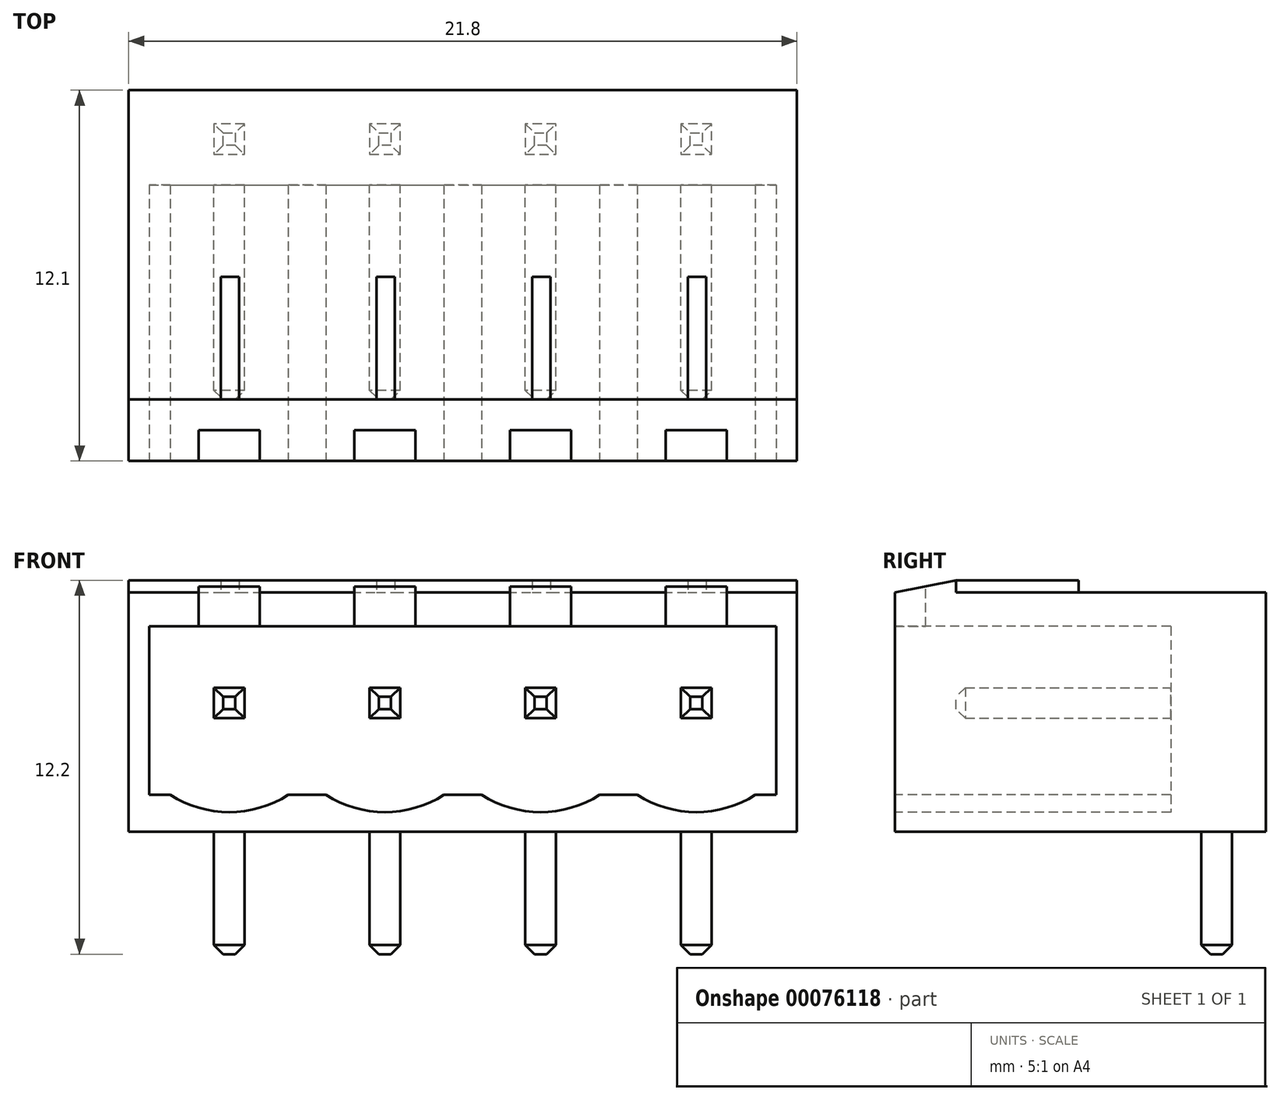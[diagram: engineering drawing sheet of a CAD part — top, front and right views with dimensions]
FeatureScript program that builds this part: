
annotation { "Feature Type Name" : "Feature", "Feature Type Description" : "" }
export const myFeature = defineFeature(function(context is Context, id is Id, definition is map)
    precondition{}
    {
        {
            var Q0;
            Q0=qCreatedBy(makeId("Front.planeOp"),FACE);
            var sketch = newSketch(context, id + "F0", { "sketchPlane" : qUnion([Q0])});
            skLineSegment(sketch, "E0.bottom", {"start": v(-10.9, 4.1) * mm, "end": v(10.9, 4.1) * mm});
            skLineSegment(sketch, "E0.top", {"start": v(-10.9, -4.1) * mm, "end": v(10.9, -4.1) * mm});
            skLineSegment(sketch, "E0.left", {"start": v(-10.9, 4.1) * mm, "end": v(-10.9, -4.1) * mm});
            skLineSegment(sketch, "E0.right", {"start": v(10.9, 4.1) * mm, "end": v(10.9, -4.1) * mm});
            skPoint(sketch, "E0.middle", {"position": v(0, 0) * mm});
            skSolve(sketch);
        }
        {
            var Q0;
            Q0=makeQuery(id+"F0.imprint","IMPRINT",FACE,{"disambiguationData":[TD([[makeQuery(id+"F0.imprint","IMPRINT",EDGE,{"derivedFrom":sQuery(id+"F0.wireOp",EDGE,"E0.bottom")}),-1.0]])]});
            extrude(context, id + "F1", {"entities" : qUnion([Q0]), "depth" : 12.1 * mm, "symmetric" : true});
        }
        {
            var Q0;
            Q0=makeQuery(id+"F1.opExtrude","CAP_FACE",FACE,{"disambiguationData":[OSD([sQuery(id+"F0.wireOp",EDGE,"E0.bottom"),sQuery(id+"F0.wireOp",EDGE,"E0.top"),sQuery(id+"F0.wireOp",EDGE,"E0.left"),sQuery(id+"F0.wireOp",EDGE,"E0.right")])],"isStart":false});
            var sketch = newSketch(context, id + "F2", { "sketchPlane" : qUnion([Q0])});
            skPoint(sketch, "E1.middle", {"position": v(0, 0) * mm});
            skLineSegment(sketch, "E2.bottom", {"start": v(-10.23, 2.6) * mm, "end": v(10.23, 2.6) * mm});
            skLineSegment(sketch, "E2.top", {"start": v(-10.23, -2.4) * mm, "end": v(10.23, -2.4) * mm, "construction": true});
            skLineSegment(sketch, "E2.left", {"start": v(-10.23, 2.6) * mm, "end": v(-10.23, -2.4) * mm});
            skLineSegment(sketch, "E2.right", {"start": v(10.23, 2.6) * mm, "end": v(10.23, -2.4) * mm});
            skPoint(sketch, "E3", {"position": v(-2.54, 0.1) * mm});
            skPoint(sketch, "E4", {"position": v(-7.62, 0.1) * mm});
            skLineSegment(sketch, "E5", {"start": v(-10.23, 0.1) * mm, "end": v(10.23, 0.1) * mm, "construction": true});
            skArc(sketch, "E6", {"start": v(0, -2.4) * mm, "mid": v(-2.54, -3.46) * mm, "end": v(-5.08, -2.4) * mm});
            skArc(sketch, "E7", {"start": v(-5.08, -2.4) * mm, "mid": v(-7.62, -3.46) * mm, "end": v(-10.16, -2.4) * mm});
            skLineSegment(sketch, "E8", {"start": v(0, 12.68) * mm, "end": v(0, -9.6) * mm, "construction": true});
            skPoint(sketch, "E9", {"position": v(2.54, 0.1) * mm});
            skPoint(sketch, "E10", {"position": v(7.62, 0.1) * mm});
            skPoint(sketch, "E11", {"position": v(0, 9.54) * mm});
            skArc(sketch, "E12", {"start": v(0, -2.4) * mm, "mid": v(2.54, -3.46) * mm, "end": v(5.08, -2.4) * mm});
            skArc(sketch, "E13", {"start": v(5.08, -2.4) * mm, "mid": v(7.62, -3.46) * mm, "end": v(10.16, -2.4) * mm});
            skLineSegment(sketch, "E14", {"start": v(10.23, -2.4) * mm, "end": v(10.16, -2.4) * mm});
            skLineSegment(sketch, "E15", {"start": v(-10.16, -2.4) * mm, "end": v(-10.23, -2.4) * mm});
            skSolve(sketch);
        }
        {
            var Q0;
            Q0 = qSketchRegion(id + "F2", true);
            extrude(context, id + "F3", {"entities" : qUnion([Q0]), "operationType" : NewBodyOperationType.REMOVE, "oppositeDirection" : true, "depth" : 9 * mm});
        }
        {
            var Q0;
            Q0=makeQuery(id+"F3.boolean.opBoolean","COPY",FACE,{"derivedFrom":makeQuery(id+"F3.opExtrude","CAP_FACE",FACE,{"disambiguationData":[OSD([sQuery(id+"F2.wireOp",EDGE,"E2.bottom"),sQuery(id+"F2.wireOp",EDGE,"E2.left"),sQuery(id+"F2.wireOp",EDGE,"E2.right"),sQuery(id+"F2.wireOp",EDGE,"E6"),sQuery(id+"F2.wireOp",EDGE,"E7"),sQuery(id+"F2.wireOp",EDGE,"E12"),sQuery(id+"F2.wireOp",EDGE,"E13"),sQuery(id+"F2.wireOp",EDGE,"E14"),sQuery(id+"F2.wireOp",EDGE,"E15")])],"isStart":false})});
            var sketch = newSketch(context, id + "F4", { "sketchPlane" : qUnion([Q0])});
            skLineSegment(sketch, "E16.bottom", {"start": v(-7.12, -0.4) * mm, "end": v(-8.12, -0.4) * mm});
            skLineSegment(sketch, "E16.top", {"start": v(-7.12, 0.6) * mm, "end": v(-8.12, 0.6) * mm});
            skLineSegment(sketch, "E16.left", {"start": v(-7.12, -0.4) * mm, "end": v(-7.12, 0.6) * mm});
            skLineSegment(sketch, "E16.right", {"start": v(-8.12, -0.4) * mm, "end": v(-8.12, 0.6) * mm});
            skPoint(sketch, "E16.middle", {"position": v(-7.62, 0.1) * mm});
            skLineSegment(sketch, "E17.bottom", {"start": v(-2.04, -0.4) * mm, "end": v(-3.04, -0.4) * mm});
            skLineSegment(sketch, "E17.top", {"start": v(-2.04, 0.6) * mm, "end": v(-3.04, 0.6) * mm});
            skLineSegment(sketch, "E17.left", {"start": v(-2.04, -0.4) * mm, "end": v(-2.04, 0.6) * mm});
            skLineSegment(sketch, "E17.right", {"start": v(-3.04, -0.4) * mm, "end": v(-3.04, 0.6) * mm});
            skPoint(sketch, "E17.middle", {"position": v(-2.54, 0.1) * mm});
            skLineSegment(sketch, "E18.bottom", {"start": v(3.04, -0.4) * mm, "end": v(2.04, -0.4) * mm});
            skLineSegment(sketch, "E18.top", {"start": v(3.04, 0.6) * mm, "end": v(2.04, 0.6) * mm});
            skLineSegment(sketch, "E18.left", {"start": v(3.04, -0.4) * mm, "end": v(3.04, 0.6) * mm});
            skLineSegment(sketch, "E18.right", {"start": v(2.04, -0.4) * mm, "end": v(2.04, 0.6) * mm});
            skPoint(sketch, "E18.middle", {"position": v(2.54, 0.1) * mm});
            skLineSegment(sketch, "E19.bottom", {"start": v(8.12, -0.4) * mm, "end": v(7.12, -0.4) * mm});
            skLineSegment(sketch, "E19.top", {"start": v(8.12, 0.6) * mm, "end": v(7.12, 0.6) * mm});
            skLineSegment(sketch, "E19.left", {"start": v(8.12, -0.4) * mm, "end": v(8.12, 0.6) * mm});
            skLineSegment(sketch, "E19.right", {"start": v(7.12, -0.4) * mm, "end": v(7.12, 0.6) * mm});
            skPoint(sketch, "E19.middle", {"position": v(7.62, 0.1) * mm});
            skLineSegment(sketch, "E20", {"start": v(10.9, 0.1) * mm, "end": v(-10.9, 0.1) * mm, "construction": true});
            skPoint(sketch, "E20.startSnap0", {"position": v(10.23, 0.1) * mm});
            skPoint(sketch, "E20.endSnap0", {"position": v(-10.23, 0.1) * mm});
            skLineSegment(sketch, "E21", {"start": v(0, 4.1) * mm, "end": v(0, -4.1) * mm, "construction": true});
            skPoint(sketch, "E21.startSnap0", {"position": v(0, 2.6) * mm});
            skSolve(sketch);
        }
        {
            var Q0;
            Q0 = qSketchRegion(id + "F4", true);
            var Q1;
            Q1=makeQuery(id+"F1.opExtrude","CAP_FACE",FACE,{"disambiguationData":[OSD([sQuery(id+"F0.wireOp",EDGE,"E0.bottom"),sQuery(id+"F0.wireOp",EDGE,"E0.top"),sQuery(id+"F0.wireOp",EDGE,"E0.left"),sQuery(id+"F0.wireOp",EDGE,"E0.right")])],"isStart":false});
            extrude(context, id + "F5", {"entities" : qUnion([Q0]), "endBoundEntityFace" : qUnion([Q1]), "depth" : 7 * mm});
        }
        {
            var Q0;
            Q0=makeQuery(id+"F1.opExtrude","SWEPT_FACE",FACE,{"disambiguationData":[OSD([sQuery(id+"F0.wireOp",EDGE,"E0.top")])]});
            var sketch = newSketch(context, id + "F6", { "sketchPlane" : qUnion([Q0])});
            skLineSegment(sketch, "E22", {"start": v(0, 6.05) * mm, "end": v(0, -6.05) * mm, "construction": true});
            skLineSegment(sketch, "E23.bottom", {"start": v(-8.12, -3.95) * mm, "end": v(-7.12, -3.95) * mm});
            skLineSegment(sketch, "E23.top", {"start": v(-8.12, -4.95) * mm, "end": v(-7.12, -4.95) * mm});
            skLineSegment(sketch, "E23.left", {"start": v(-8.12, -3.95) * mm, "end": v(-8.12, -4.95) * mm});
            skLineSegment(sketch, "E23.right", {"start": v(-7.12, -3.95) * mm, "end": v(-7.12, -4.95) * mm});
            skPoint(sketch, "E23.middle", {"position": v(-7.62, -4.45) * mm});
            skLineSegment(sketch, "E24.bottom", {"start": v(-3.04, -3.95) * mm, "end": v(-2.04, -3.95) * mm});
            skLineSegment(sketch, "E24.top", {"start": v(-3.04, -4.95) * mm, "end": v(-2.04, -4.95) * mm});
            skLineSegment(sketch, "E24.left", {"start": v(-3.04, -3.95) * mm, "end": v(-3.04, -4.95) * mm});
            skLineSegment(sketch, "E24.right", {"start": v(-2.04, -3.95) * mm, "end": v(-2.04, -4.95) * mm});
            skPoint(sketch, "E24.middle", {"position": v(-2.54, -4.45) * mm});
            skLineSegment(sketch, "E25", {"start": v(-10.9, -4.45) * mm, "end": v(10.9, -4.45) * mm, "construction": true});
            skPoint(sketch, "E25.startSnap0", {"position": v(-8.12, -4.45) * mm});
            skLineSegment(sketch, "E26.MirrorCS", {"start": v(8.12, -3.95) * mm, "end": v(8.12, -4.95) * mm});
            skLineSegment(sketch, "E27.MirrorCS", {"start": v(7.12, -3.95) * mm, "end": v(7.12, -4.95) * mm});
            skLineSegment(sketch, "E28.MirrorCS", {"start": v(3.04, -3.95) * mm, "end": v(2.04, -3.95) * mm});
            skLineSegment(sketch, "E29.MirrorCS", {"start": v(3.04, -4.95) * mm, "end": v(2.04, -4.95) * mm});
            skLineSegment(sketch, "E30.MirrorCS", {"start": v(8.12, -4.95) * mm, "end": v(7.12, -4.95) * mm});
            skPoint(sketch, "E31.MirrorP", {"position": v(2.54, -4.45) * mm});
            skLineSegment(sketch, "E32.MirrorCS", {"start": v(3.04, -3.95) * mm, "end": v(3.04, -4.95) * mm});
            skLineSegment(sketch, "E33.MirrorCS", {"start": v(2.04, -3.95) * mm, "end": v(2.04, -4.95) * mm});
            skPoint(sketch, "E34.MirrorP", {"position": v(8.12, -4.45) * mm});
            skPoint(sketch, "E35.MirrorP", {"position": v(7.62, -4.45) * mm});
            skLineSegment(sketch, "E36.MirrorCS", {"start": v(8.12, -3.95) * mm, "end": v(7.12, -3.95) * mm});
            skSolve(sketch);
        }
        {
            var Q0;
            Q0 = qSketchRegion(id + "F6", true);
            extrude(context, id + "F7", {"entities" : qUnion([Q0]), "depth" : 4 * mm});
        }
        {
            var Q0;
            Q0=makeQuery(id+"F1.opExtrude","SWEPT_FACE",FACE,{"disambiguationData":[OSD([sQuery(id+"F0.wireOp",EDGE,"E0.bottom")])]});
            var sketch = newSketch(context, id + "F8", { "sketchPlane" : qUnion([Q0])});
            skLineSegment(sketch, "E37", {"start": v(0, 6.05) * mm, "end": v(0, -6.05) * mm, "construction": true});
            skLineSegment(sketch, "E38.bottom", {"start": v(-3.54, -5.05) * mm, "end": v(-1.54, -5.05) * mm});
            skLineSegment(sketch, "E38.top", {"start": v(-3.54, -6.05) * mm, "end": v(-1.54, -6.05) * mm});
            skLineSegment(sketch, "E38.left", {"start": v(-3.54, -5.05) * mm, "end": v(-3.54, -6.05) * mm});
            skLineSegment(sketch, "E38.right", {"start": v(-1.54, -5.05) * mm, "end": v(-1.54, -6.05) * mm});
            skPoint(sketch, "E38.middle", {"position": v(-2.54, -5.55) * mm});
            skLineSegment(sketch, "E39.1.0.0", {"start": v(3.54, -5.05) * mm, "end": v(3.54, -6.05) * mm});
            skLineSegment(sketch, "E39.1.0.1", {"start": v(1.54, -5.05) * mm, "end": v(1.54, -6.05) * mm});
            skLineSegment(sketch, "E39.1.0.2", {"start": v(1.54, -6.05) * mm, "end": v(3.54, -6.05) * mm});
            skLineSegment(sketch, "E39.1.0.3", {"start": v(1.54, -5.05) * mm, "end": v(3.54, -5.05) * mm});
            skPoint(sketch, "E39.1.0.4", {"position": v(2.54, -5.55) * mm});
            skLineSegment(sketch, "E39.2.0.0", {"start": v(8.62, -5.05) * mm, "end": v(8.62, -6.05) * mm});
            skLineSegment(sketch, "E39.2.0.1", {"start": v(6.62, -5.05) * mm, "end": v(6.62, -6.05) * mm});
            skLineSegment(sketch, "E39.2.0.2", {"start": v(6.62, -6.05) * mm, "end": v(8.62, -6.05) * mm});
            skLineSegment(sketch, "E39.2.0.3", {"start": v(6.62, -5.05) * mm, "end": v(8.62, -5.05) * mm});
            skPoint(sketch, "E39.2.0.4", {"position": v(7.62, -5.55) * mm});
            skLineSegment(sketch, "E39.direction1", {"start": v(-1.54, -6.05) * mm, "end": v(3.54, -6.05) * mm, "construction": true});
            skLineSegment(sketch, "E40.1.0.0", {"start": v(-8.62, -5.05) * mm, "end": v(-6.62, -5.05) * mm});
            skLineSegment(sketch, "E40.1.0.1", {"start": v(-8.62, -6.05) * mm, "end": v(-6.62, -6.05) * mm});
            skLineSegment(sketch, "E40.1.0.2", {"start": v(-8.62, -5.05) * mm, "end": v(-8.62, -6.05) * mm});
            skLineSegment(sketch, "E40.1.0.3", {"start": v(-6.62, -5.05) * mm, "end": v(-6.62, -6.05) * mm});
            skPoint(sketch, "E40.1.0.4", {"position": v(-7.62, -5.55) * mm});
            skLineSegment(sketch, "E40.direction1", {"start": v(-3.54, -5.05) * mm, "end": v(-8.62, -5.05) * mm, "construction": true});
            skSolve(sketch);
        }
        {
            var Q0;
            Q0 = qSketchRegion(id + "F8", true);
            extrude(context, id + "F9", {"entities" : qUnion([Q0]), "operationType" : NewBodyOperationType.REMOVE, "oppositeDirection" : true, "depth" : 2 * mm});
        }
        {
            var Q0;
            {var subQ0=sQuery(id+"F0.wireOp",EDGE,"E0.top");var subQ1=sQuery(id+"F0.wireOp",EDGE,"E0.bottom");var subQ2=sQuery(id+"F0.wireOp",EDGE,"E0.left");var subQ3=sQuery(id+"F0.wireOp",EDGE,"E0.right");Q0=makeQuery(id+"F9.boolean.opBoolean","SPLIT",FACE,{"disambiguationData":[TD([makeQuery(id+"F1.opExtrude","SWEPT_FACE",FACE,{"disambiguationData":[OSD([subQ0])]})])],"derivedFrom":makeQuery(id+"F1.opExtrude","CAP_FACE",FACE,{"disambiguationData":[OSD([subQ1,subQ0,subQ2,subQ3])],"isStart":false})});}
            var sketch = newSketch(context, id + "F10", { "sketchPlane" : qUnion([Q0])});
            skLineSegment(sketch, "E41.bottom", {"start": v(-10.23, -2.4) * mm, "end": v(10.23, -2.4) * mm});
            skLineSegment(sketch, "E41.top", {"start": v(-10.23, -2.9) * mm, "end": v(10.23, -2.9) * mm});
            skLineSegment(sketch, "E41.left", {"start": v(-10.23, -2.4) * mm, "end": v(-10.23, -2.9) * mm});
            skLineSegment(sketch, "E41.right", {"start": v(10.23, -2.4) * mm, "end": v(10.23, -2.9) * mm});
            skSolve(sketch);
        }
        {
            var Q0;
            Q0 = qSketchRegion(id + "F10", true);
            var Q1;
            Q1=makeQuery(id+"F3.boolean.opBoolean","COPY",FACE,{"derivedFrom":makeQuery(id+"F3.opExtrude","CAP_FACE",FACE,{"disambiguationData":[OSD([sQuery(id+"F2.wireOp",EDGE,"E2.bottom"),sQuery(id+"F2.wireOp",EDGE,"E2.left"),sQuery(id+"F2.wireOp",EDGE,"E2.right"),sQuery(id+"F2.wireOp",EDGE,"E6"),sQuery(id+"F2.wireOp",EDGE,"E7"),sQuery(id+"F2.wireOp",EDGE,"E12"),sQuery(id+"F2.wireOp",EDGE,"E13"),sQuery(id+"F2.wireOp",EDGE,"E14"),sQuery(id+"F2.wireOp",EDGE,"E15")])],"isStart":false})});
            extrude(context, id + "F11", {"entities" : qUnion([Q0]), "operationType" : NewBodyOperationType.REMOVE, "endBound" : BoundingType.UP_TO_SURFACE, "oppositeDirection" : true, "endBoundEntityFace" : qUnion([Q1]), "depth" : 25 * mm});
        }
        {
            var Q0;
            Q0=makeQuery(id+"F5.opExtrude","CAP_FACE",FACE,{"disambiguationData":[OSD([sQuery(id+"F4.wireOp",EDGE,"E16.bottom"),sQuery(id+"F4.wireOp",EDGE,"E16.top"),sQuery(id+"F4.wireOp",EDGE,"E16.left"),sQuery(id+"F4.wireOp",EDGE,"E16.right")])],"isStart":false});
            var Q1;
            Q1=makeQuery(id+"F5.opExtrude","CAP_FACE",FACE,{"disambiguationData":[OSD([sQuery(id+"F4.wireOp",EDGE,"E17.bottom"),sQuery(id+"F4.wireOp",EDGE,"E17.top"),sQuery(id+"F4.wireOp",EDGE,"E17.left"),sQuery(id+"F4.wireOp",EDGE,"E17.right")])],"isStart":false});
            var Q2;
            Q2=makeQuery(id+"F5.opExtrude","CAP_FACE",FACE,{"disambiguationData":[OSD([sQuery(id+"F4.wireOp",EDGE,"E18.bottom"),sQuery(id+"F4.wireOp",EDGE,"E18.top"),sQuery(id+"F4.wireOp",EDGE,"E18.left"),sQuery(id+"F4.wireOp",EDGE,"E18.right")])],"isStart":false});
            var Q3;
            Q3=makeQuery(id+"F5.opExtrude","CAP_FACE",FACE,{"disambiguationData":[OSD([sQuery(id+"F4.wireOp",EDGE,"E19.bottom"),sQuery(id+"F4.wireOp",EDGE,"E19.top"),sQuery(id+"F4.wireOp",EDGE,"E19.left"),sQuery(id+"F4.wireOp",EDGE,"E19.right")])],"isStart":false});
            var Q4;
            Q4=makeQuery(id+"F7.opExtrude","CAP_FACE",FACE,{"disambiguationData":[OSD([sQuery(id+"F6.wireOp",EDGE,"E23.bottom"),sQuery(id+"F6.wireOp",EDGE,"E23.top"),sQuery(id+"F6.wireOp",EDGE,"E23.left"),sQuery(id+"F6.wireOp",EDGE,"E23.right")])],"isStart":false});
            var Q5;
            Q5=makeQuery(id+"F7.opExtrude","CAP_FACE",FACE,{"disambiguationData":[OSD([sQuery(id+"F6.wireOp",EDGE,"E24.bottom"),sQuery(id+"F6.wireOp",EDGE,"E24.top"),sQuery(id+"F6.wireOp",EDGE,"E24.left"),sQuery(id+"F6.wireOp",EDGE,"E24.right")])],"isStart":false});
            var Q6;
            Q6=makeQuery(id+"F7.opExtrude","CAP_FACE",FACE,{"disambiguationData":[OSD([sQuery(id+"F6.wireOp",EDGE,"E28.MirrorCS"),sQuery(id+"F6.wireOp",EDGE,"E29.MirrorCS"),sQuery(id+"F6.wireOp",EDGE,"E32.MirrorCS"),sQuery(id+"F6.wireOp",EDGE,"E33.MirrorCS")])],"isStart":false});
            var Q7;
            Q7=makeQuery(id+"F7.opExtrude","CAP_FACE",FACE,{"disambiguationData":[OSD([sQuery(id+"F6.wireOp",EDGE,"E26.MirrorCS"),sQuery(id+"F6.wireOp",EDGE,"E27.MirrorCS"),sQuery(id+"F6.wireOp",EDGE,"E30.MirrorCS"),sQuery(id+"F6.wireOp",EDGE,"E36.MirrorCS")])],"isStart":false});
            chamfer(context, id + "F12", {"entities" : qUnion([Q0, Q1, Q2, Q3, Q4, Q5, Q6, Q7]), "width" : 0.3 * mm, "tangentPropagation" : true});
        }
        {
            var Q0;
            Q0=makeQuery(id+"F1.opExtrude","SWEPT_FACE",FACE,{"disambiguationData":[OSD([sQuery(id+"F0.wireOp",EDGE,"E0.right")])]});
            var sketch = newSketch(context, id + "F13", { "sketchPlane" : qUnion([Q0])});
            skLineSegment(sketch, "E42", {"start": v(-6.05, 4.1) * mm, "end": v(-6.05, 3.7) * mm});
            skLineSegment(sketch, "E43", {"start": v(-6.05, 3.7) * mm, "end": v(-4.05, 4.1) * mm});
            skLineSegment(sketch, "E44", {"start": v(-4.05, 4.1) * mm, "end": v(-6.05, 4.1) * mm});
            skLineSegment(sketch, "E45", {"start": v(-4.05, 4.1) * mm, "end": v(-4.05, 3.7) * mm});
            skLineSegment(sketch, "E46", {"start": v(-4.05, 3.7) * mm, "end": v(6.05, 3.7) * mm});
            skLineSegment(sketch, "E47", {"start": v(6.05, 3.7) * mm, "end": v(6.05, 4.1) * mm});
            skLineSegment(sketch, "E48", {"start": v(6.05, 4.1) * mm, "end": v(-4.05, 4.1) * mm});
            skSolve(sketch);
        }
        {
            var Q0;
            Q0 = qSketchRegion(id + "F13", true);
            extrude(context, id + "F14", {"entities" : qUnion([Q0]), "operationType" : NewBodyOperationType.REMOVE, "endBound" : BoundingType.THROUGH_ALL, "oppositeDirection" : true, "depth" : 25 * mm});
        }
        {
            var Q0;
            Q0=makeQuery(id+"F14.boolean.opBoolean","COPY",FACE,{"derivedFrom":makeQuery(id+"F14.opExtrude","SWEPT_FACE",FACE,{"disambiguationData":[OSD([sQuery(id+"F13.wireOp",EDGE,"E46")])]})});
            var sketch = newSketch(context, id + "F15", { "sketchPlane" : qUnion([Q0])});
            skLineSegment(sketch, "E49.bottom", {"start": v(-7.9, -4.05) * mm, "end": v(-7.3, -4.05) * mm});
            skLineSegment(sketch, "E49.top", {"start": v(-7.9, -0.05) * mm, "end": v(-7.3, -0.05) * mm});
            skLineSegment(sketch, "E49.left", {"start": v(-7.9, -4.05) * mm, "end": v(-7.9, -0.05) * mm});
            skLineSegment(sketch, "E49.right", {"start": v(-7.3, -4.05) * mm, "end": v(-7.3, -0.05) * mm});
            skLineSegment(sketch, "E50.1.0.0", {"start": v(-2.82, -4.05) * mm, "end": v(-2.22, -4.05) * mm});
            skLineSegment(sketch, "E50.1.0.1", {"start": v(-2.82, -0.05) * mm, "end": v(-2.22, -0.05) * mm});
            skLineSegment(sketch, "E50.1.0.2", {"start": v(-2.82, -4.05) * mm, "end": v(-2.82, -0.05) * mm});
            skLineSegment(sketch, "E50.1.0.3", {"start": v(-2.22, -4.05) * mm, "end": v(-2.22, -0.05) * mm});
            skLineSegment(sketch, "E50.2.0.0", {"start": v(2.26, -4.05) * mm, "end": v(2.86, -4.05) * mm});
            skLineSegment(sketch, "E50.2.0.1", {"start": v(2.26, -0.05) * mm, "end": v(2.86, -0.05) * mm});
            skLineSegment(sketch, "E50.2.0.2", {"start": v(2.26, -4.05) * mm, "end": v(2.26, -0.05) * mm});
            skLineSegment(sketch, "E50.2.0.3", {"start": v(2.86, -4.05) * mm, "end": v(2.86, -0.05) * mm});
            skLineSegment(sketch, "E50.3.0.0", {"start": v(7.34, -4.05) * mm, "end": v(7.94, -4.05) * mm});
            skLineSegment(sketch, "E50.3.0.1", {"start": v(7.34, -0.05) * mm, "end": v(7.94, -0.05) * mm});
            skLineSegment(sketch, "E50.3.0.2", {"start": v(7.34, -4.05) * mm, "end": v(7.34, -0.05) * mm});
            skLineSegment(sketch, "E50.3.0.3", {"start": v(7.94, -4.05) * mm, "end": v(7.94, -0.05) * mm});
            skLineSegment(sketch, "E50.direction1", {"start": v(-7.9, -4.05) * mm, "end": v(-2.82, -4.05) * mm, "construction": true});
            skSolve(sketch);
        }
        {
            var Q0;
            Q0 = qSketchRegion(id + "F15", true);
            extrude(context, id + "F16", {"entities" : qUnion([Q0]), "operationType" : NewBodyOperationType.ADD, "depth" : 0.4 * mm});
        }
    });
